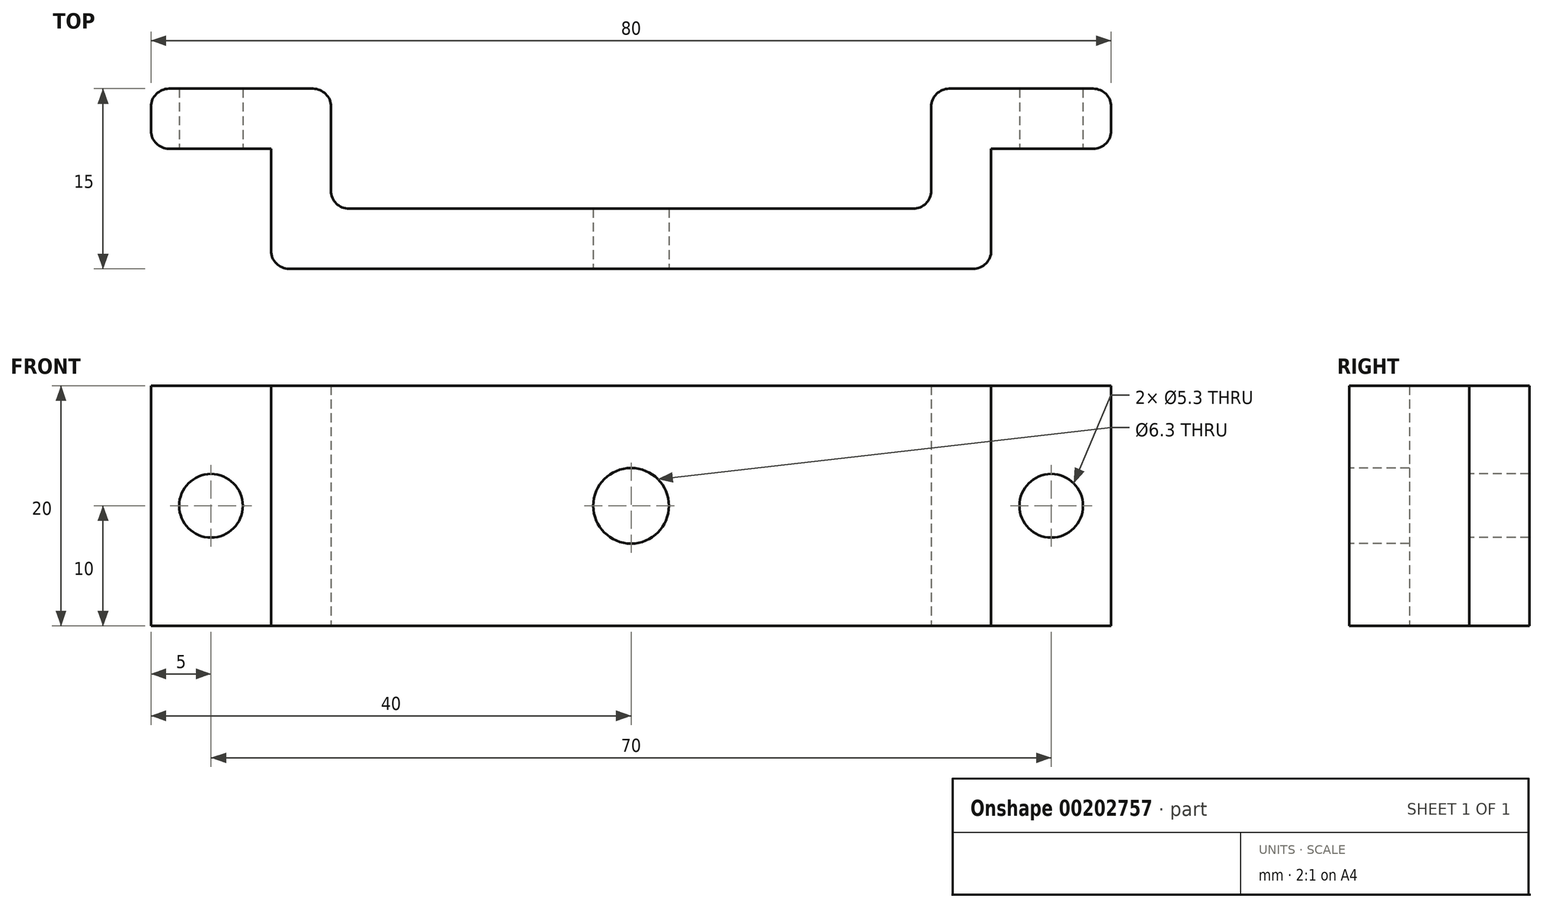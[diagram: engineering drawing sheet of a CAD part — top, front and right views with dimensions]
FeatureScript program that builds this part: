
annotation { "Feature Type Name" : "Feature", "Feature Type Description" : "" }
export const myFeature = defineFeature(function(context is Context, id is Id, definition is map)
    precondition{}
    {
        {
            var Q0;
            Q0=qCreatedBy(makeId("Top.planeOp"),FACE);
            var sketch = newSketch(context, id + "F0", { "sketchPlane" : qUnion([Q0])});
            skLineSegment(sketch, "E0.bottom", {"start": v(30, 7.5) * mm, "end": v(-30, 7.5) * mm});
            skLineSegment(sketch, "E0.top", {"start": v(30, -7.5) * mm, "end": v(-30, -7.5) * mm});
            skLineSegment(sketch, "E0.left", {"start": v(30, 7.5) * mm, "end": v(30, -7.5) * mm});
            skLineSegment(sketch, "E0.right", {"start": v(-30, 7.5) * mm, "end": v(-30, -7.5) * mm});
            skPoint(sketch, "E0.middle", {"position": v(0, 0) * mm});
            skLineSegment(sketch, "E1.bottom", {"start": v(-25, 7.5) * mm, "end": v(25, 7.5) * mm});
            skLineSegment(sketch, "E1.top", {"start": v(-25, -2.5) * mm, "end": v(25, -2.5) * mm});
            skLineSegment(sketch, "E1.left", {"start": v(-25, 7.5) * mm, "end": v(-25, -2.5) * mm});
            skLineSegment(sketch, "E1.right", {"start": v(25, 7.5) * mm, "end": v(25, -2.5) * mm});
            skLineSegment(sketch, "E2.bottom", {"start": v(30, 7.5) * mm, "end": v(40, 7.5) * mm});
            skLineSegment(sketch, "E2.top", {"start": v(30, 2.5) * mm, "end": v(40, 2.5) * mm});
            skLineSegment(sketch, "E2.left", {"start": v(30, 7.5) * mm, "end": v(30, 2.5) * mm});
            skLineSegment(sketch, "E2.right", {"start": v(40, 7.5) * mm, "end": v(40, 2.5) * mm});
            skLineSegment(sketch, "E3.bottom", {"start": v(-30, 7.5) * mm, "end": v(-40, 7.5) * mm});
            skLineSegment(sketch, "E3.top", {"start": v(-30, 2.5) * mm, "end": v(-40, 2.5) * mm});
            skLineSegment(sketch, "E3.left", {"start": v(-30, 7.5) * mm, "end": v(-30, 2.5) * mm});
            skLineSegment(sketch, "E3.right", {"start": v(-40, 7.5) * mm, "end": v(-40, 2.5) * mm});
            skSolve(sketch);
        }
        {
            var Q0;
            Q0=makeQuery(id+"F0.imprint","IMPRINT",FACE,{"disambiguationData":[TD([[makeQuery(id+"F0.imprint","IMPRINT",EDGE,{"derivedFrom":sQuery(id+"F0.wireOp",EDGE,"E3.bottom")}),1.0]])]});
            var Q1;
            Q1=makeQuery(id+"F0.imprint","IMPRINT",FACE,{"disambiguationData":[TD([[makeQuery(id+"F0.imprint","IMPRINT",EDGE,{"derivedFrom":sQuery(id+"F0.wireOp",EDGE,"E0.top")}),-1.0]])]});
            var Q2;
            Q2=makeQuery(id+"F0.imprint","IMPRINT",FACE,{"disambiguationData":[TD([[makeQuery(id+"F0.imprint","IMPRINT",EDGE,{"derivedFrom":sQuery(id+"F0.wireOp",EDGE,"E2.bottom")}),-1.0]])]});
            extrude(context, id + "F1", {"entities" : qUnion([Q0, Q1, Q2]), "depth" : 20 * mm});
        }
        {
            var Q0;
            Q0=makeQuery(id+"F1.opExtrude","SWEPT_FACE",FACE,{"disambiguationData":[OSD([sQuery(id+"F0.wireOp",EDGE,"E0.top")])]});
            var sketch = newSketch(context, id + "F2", { "sketchPlane" : qUnion([Q0])});
            skCircle(sketch, "E4", {"center": v(0, 10) * mm, "radius": 3.15 * mm});
            skSolve(sketch);
        }
        {
            var Q0;
            Q0=makeQuery(id+"F2.imprint","IMPRINT",FACE,{"disambiguationData":[TD([[makeQuery(id+"F2.imprint","IMPRINT",EDGE,{"derivedFrom":sQuery(id+"F2.wireOp",EDGE,"E4")}),1.0]])]});
            extrude(context, id + "F3", {"entities" : qUnion([Q0]), "operationType" : NewBodyOperationType.REMOVE, "oppositeDirection" : true, "depth" : 25 * mm});
        }
        {
            var Q0;
            Q0=makeQuery(id+"F1.opExtrude","SWEPT_FACE",FACE,{"disambiguationData":[OSD([sQuery(id+"F0.wireOp",EDGE,"E3.top")])]});
            var sketch = newSketch(context, id + "F4", { "sketchPlane" : qUnion([Q0])});
            skCircle(sketch, "E5", {"center": v(-35, 10) * mm, "radius": 2.65 * mm});
            skCircle(sketch, "E6", {"center": v(35, 10) * mm, "radius": 2.65 * mm});
            skSolve(sketch);
        }
        {
            var Q0;
            Q0=makeQuery(id+"F4.imprint","IMPRINT",FACE,{"disambiguationData":[TD([[makeQuery(id+"F4.imprint","IMPRINT",EDGE,{"derivedFrom":sQuery(id+"F4.wireOp",EDGE,"E5")}),1.0]])]});
            var Q1;
            Q1=makeQuery(id+"F4.imprint","IMPRINT",FACE,{"disambiguationData":[TD([[makeQuery(id+"F4.imprint","IMPRINT",EDGE,{"derivedFrom":sQuery(id+"F4.wireOp",EDGE,"E6")}),1.0]])]});
            extrude(context, id + "F5", {"entities" : qUnion([Q0, Q1]), "operationType" : NewBodyOperationType.REMOVE, "oppositeDirection" : true, "depth" : 25 * mm});
        }
        {
            var Q0;
            Q0=makeQuery(id+"F1.opExtrude","SWEPT_EDGE",EDGE,{"disambiguationData":[OSD([sQuery(id+"F0.wireOp",EDGE,"E1.top"),sQuery(id+"F0.wireOp",EDGE,"E1.left")])]});
            var Q1;
            Q1=makeQuery(id+"F1.opExtrude","SWEPT_EDGE",EDGE,{"disambiguationData":[OSD([sQuery(id+"F0.wireOp",EDGE,"E1.top"),sQuery(id+"F0.wireOp",EDGE,"E1.right")])]});
            var Q2;
            Q2=makeQuery(id+"F1.opExtrude","SWEPT_EDGE",EDGE,{"disambiguationData":[OSD([sQuery(id+"F0.wireOp",EDGE,"E2.bottom"),sQuery(id+"F0.wireOp",EDGE,"E2.right")])]});
            var Q3;
            Q3=makeQuery(id+"F1.opExtrude","SWEPT_EDGE",EDGE,{"disambiguationData":[OSD([sQuery(id+"F0.wireOp",EDGE,"E2.top"),sQuery(id+"F0.wireOp",EDGE,"E2.right")])]});
            var Q4;
            Q4=makeQuery(id+"F1.opExtrude","SWEPT_EDGE",EDGE,{"disambiguationData":[OSD([sQuery(id+"F0.wireOp",EDGE,"E0.top"),sQuery(id+"F0.wireOp",EDGE,"E0.left")])]});
            var Q5;
            Q5=makeQuery(id+"F1.opExtrude","SWEPT_EDGE",EDGE,{"disambiguationData":[OSD([sQuery(id+"F0.wireOp",EDGE,"E0.top"),sQuery(id+"F0.wireOp",EDGE,"E0.right")])]});
            var Q6;
            Q6=makeQuery(id+"F1.opExtrude","SWEPT_EDGE",EDGE,{"disambiguationData":[OSD([sQuery(id+"F0.wireOp",EDGE,"E3.top"),sQuery(id+"F0.wireOp",EDGE,"E3.right")])]});
            var Q7;
            Q7=makeQuery(id+"F1.opExtrude","SWEPT_EDGE",EDGE,{"disambiguationData":[OSD([sQuery(id+"F0.wireOp",EDGE,"E3.bottom"),sQuery(id+"F0.wireOp",EDGE,"E3.right")])]});
            var Q8;
            Q8=makeQuery(id+"F1.opExtrude","SWEPT_EDGE",EDGE,{"disambiguationData":[OSD([sQuery(id+"F0.wireOp",EDGE,"E0.bottom"),sQuery(id+"F0.wireOp",EDGE,"E1.bottom"),sQuery(id+"F0.wireOp",EDGE,"E1.left")])]});
            var Q9;
            Q9=makeQuery(id+"F1.opExtrude","SWEPT_EDGE",EDGE,{"disambiguationData":[OSD([sQuery(id+"F0.wireOp",EDGE,"E0.bottom"),sQuery(id+"F0.wireOp",EDGE,"E1.bottom"),sQuery(id+"F0.wireOp",EDGE,"E1.right")])]});
            fillet(context, id + "F6", {"entities" : qUnion([Q0, Q1, Q2, Q3, Q4, Q5, Q6, Q7, Q8, Q9]), "radius" : 1.5 * mm, "tangentPropagation" : true, "allowEdgeOverflow" : false});
        }
    });
